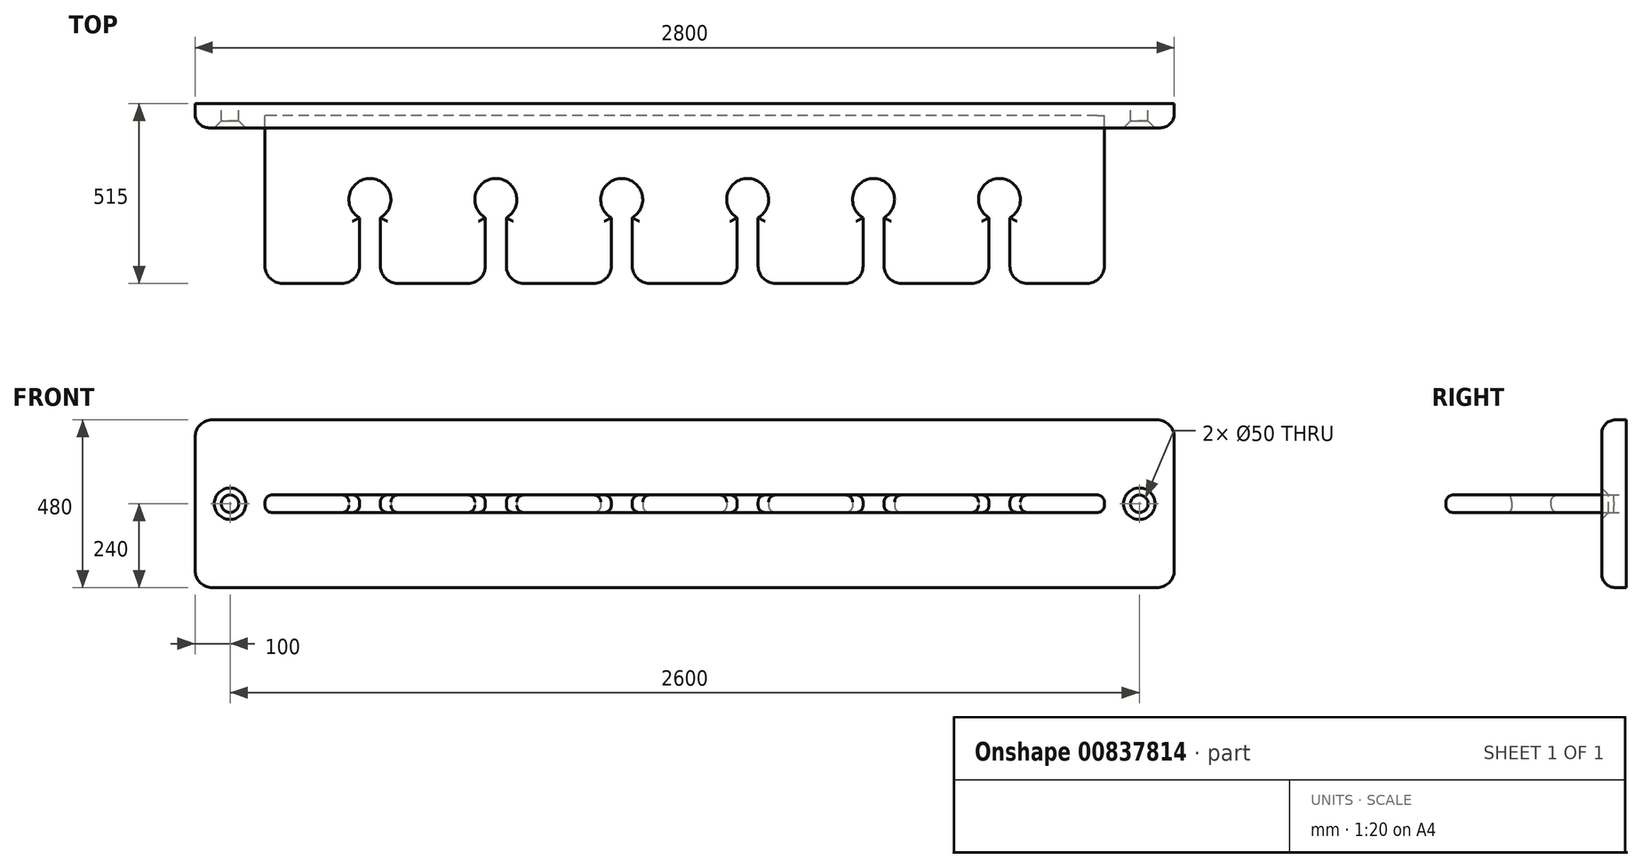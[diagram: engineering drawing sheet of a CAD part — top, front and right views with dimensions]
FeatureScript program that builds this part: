
annotation { "Feature Type Name" : "Feature", "Feature Type Description" : "" }
export const myFeature = defineFeature(function(context is Context, id is Id, definition is map)
    precondition{}
    {
        {
            assignVariable(context, id + "F0", {"name" : "size", "anyValue" : 2400 * mm});
        }
        {
            assignVariable(context, id + "F1", {"name" : "ratio", "anyValue" : 1 / 5});
        }
        {
            assignVariable(context, id + "F2", {"name" : "height", "anyValue" : getVariable(context, 'size') * getVariable(context, 'ratio')});
        }
        {
            assignVariable(context, id + "F3", {"name" : "thick", "anyValue" : 50 * mm});
        }
        {
            assignVariable(context, id + "F4", {"name" : "round", "anyValue" : 20 * mm});
        }
        {
            var Q0;
            Q0=qCreatedBy(makeId("Top.planeOp"),FACE);
            var sketch = newSketch(context, id + "F5", { "sketchPlane" : qUnion([Q0])});
            skLineSegment(sketch, "E0.top", {"start": v(1200, 240) * mm, "end": v(-1200, 240) * mm});
            skLineSegment(sketch, "E0.left", {"start": v(1200, -190) * mm, "end": v(1200, 240) * mm});
            skLineSegment(sketch, "E0.right", {"start": v(-1200, -190) * mm, "end": v(-1200, 240) * mm});
            skPoint(sketch, "E0.middle", {"position": v(0, 0) * mm});
            skArc(sketch, "E1", {"start": v(-870, -51.96) * mm, "mid": v(-900, 60) * mm, "end": v(-930, -51.96) * mm});
            skLineSegment(sketch, "E2", {"start": v(-930, -51.96) * mm, "end": v(-930, -190) * mm});
            skLineSegment(sketch, "E3", {"start": v(-870, -51.96) * mm, "end": v(-870, -190) * mm});
            skLineSegment(sketch, "E4.trimOffspring", {"start": v(-980, -240) * mm, "end": v(-1150, -240) * mm});
            skArc(sketch, "E5.1.0.0", {"start": v(-510, -51.96) * mm, "mid": v(-540, 60) * mm, "end": v(-570, -51.96) * mm});
            skLineSegment(sketch, "E5.1.0.1", {"start": v(-510, -51.96) * mm, "end": v(-510, -190) * mm});
            skLineSegment(sketch, "E5.1.0.2", {"start": v(-570, -51.96) * mm, "end": v(-570, -190) * mm});
            skArc(sketch, "E5.2.0.0", {"start": v(-150, -51.96) * mm, "mid": v(-180, 60) * mm, "end": v(-210, -51.96) * mm});
            skLineSegment(sketch, "E5.2.0.1", {"start": v(-150, -51.96) * mm, "end": v(-150, -190) * mm});
            skLineSegment(sketch, "E5.2.0.2", {"start": v(-210, -51.96) * mm, "end": v(-210, -190) * mm});
            skArc(sketch, "E5.3.0.0", {"start": v(210, -51.96) * mm, "mid": v(180, 60) * mm, "end": v(150, -51.96) * mm});
            skLineSegment(sketch, "E5.3.0.1", {"start": v(210, -51.96) * mm, "end": v(210, -190) * mm});
            skLineSegment(sketch, "E5.3.0.2", {"start": v(150, -51.96) * mm, "end": v(150, -190) * mm});
            skArc(sketch, "E5.4.0.0", {"start": v(570, -51.96) * mm, "mid": v(540, 60) * mm, "end": v(510, -51.96) * mm});
            skLineSegment(sketch, "E5.4.0.1", {"start": v(570, -51.96) * mm, "end": v(570, -190) * mm});
            skLineSegment(sketch, "E5.4.0.2", {"start": v(510, -51.96) * mm, "end": v(510, -190) * mm});
            skArc(sketch, "E5.5.0.0", {"start": v(930, -51.96) * mm, "mid": v(900, 60) * mm, "end": v(870, -51.96) * mm});
            skLineSegment(sketch, "E5.5.0.1", {"start": v(930, -51.96) * mm, "end": v(930, -190) * mm});
            skLineSegment(sketch, "E5.5.0.2", {"start": v(870, -51.96) * mm, "end": v(870, -190) * mm});
            skLineSegment(sketch, "E5.direction1", {"start": v(-900, 0) * mm, "end": v(-540, 0) * mm, "construction": true});
            skLineSegment(sketch, "E6.trimOffspring", {"start": v(-620, -240) * mm, "end": v(-820, -240) * mm});
            skLineSegment(sketch, "E7.trimOffspring", {"start": v(-260, -240) * mm, "end": v(-460, -240) * mm});
            skLineSegment(sketch, "E8.trimOffspring", {"start": v(100, -240) * mm, "end": v(-100, -240) * mm});
            skLineSegment(sketch, "E9.trimOffspring", {"start": v(460, -240) * mm, "end": v(260, -240) * mm});
            skLineSegment(sketch, "E10.trimOffspring", {"start": v(820, -240) * mm, "end": v(620, -240) * mm});
            skLineSegment(sketch, "E11", {"start": v(1150, -240) * mm, "end": v(980, -240) * mm});
            skPoint(sketch, "E12.visualSharp", {"position": v(-930, -240) * mm});
            skArc(sketch, "E12.filletArc", {"start": v(-980, -240) * mm, "mid": v(-944.64, -225.36) * mm, "end": v(-930, -190) * mm});
            skPoint(sketch, "E13.visualSharp", {"position": v(-870, -240) * mm});
            skArc(sketch, "E13.filletArc", {"start": v(-870, -190) * mm, "mid": v(-855.36, -225.36) * mm, "end": v(-820, -240) * mm});
            skPoint(sketch, "E14.visualSharp", {"position": v(-570, -240) * mm});
            skArc(sketch, "E14.filletArc", {"start": v(-620, -240) * mm, "mid": v(-584.64, -225.36) * mm, "end": v(-570, -190) * mm});
            skPoint(sketch, "E15.visualSharp", {"position": v(-510, -240) * mm});
            skArc(sketch, "E15.filletArc", {"start": v(-510, -190) * mm, "mid": v(-495.36, -225.36) * mm, "end": v(-460, -240) * mm});
            skPoint(sketch, "E16.visualSharp", {"position": v(-210, -240) * mm});
            skArc(sketch, "E16.filletArc", {"start": v(-260, -240) * mm, "mid": v(-224.64, -225.36) * mm, "end": v(-210, -190) * mm});
            skPoint(sketch, "E17.visualSharp", {"position": v(-150, -240) * mm});
            skArc(sketch, "E17.filletArc", {"start": v(-150, -190) * mm, "mid": v(-135.36, -225.36) * mm, "end": v(-100, -240) * mm});
            skPoint(sketch, "E18.visualSharp", {"position": v(150, -240) * mm});
            skArc(sketch, "E18.filletArc", {"start": v(100, -240) * mm, "mid": v(135.36, -225.36) * mm, "end": v(150, -190) * mm});
            skPoint(sketch, "E19.visualSharp", {"position": v(210, -240) * mm});
            skArc(sketch, "E19.filletArc", {"start": v(210, -190) * mm, "mid": v(224.64, -225.36) * mm, "end": v(260, -240) * mm});
            skPoint(sketch, "E20.visualSharp", {"position": v(510, -240) * mm});
            skArc(sketch, "E20.filletArc", {"start": v(460, -240) * mm, "mid": v(495.36, -225.36) * mm, "end": v(510, -190) * mm});
            skPoint(sketch, "E21.visualSharp", {"position": v(570, -240) * mm});
            skArc(sketch, "E21.filletArc", {"start": v(570, -190) * mm, "mid": v(584.64, -225.36) * mm, "end": v(620, -240) * mm});
            skPoint(sketch, "E22.visualSharp", {"position": v(870, -240) * mm});
            skArc(sketch, "E22.filletArc", {"start": v(820, -240) * mm, "mid": v(855.36, -225.36) * mm, "end": v(870, -190) * mm});
            skPoint(sketch, "E23.visualSharp", {"position": v(930, -240) * mm});
            skArc(sketch, "E23.filletArc", {"start": v(930, -190) * mm, "mid": v(944.64, -225.36) * mm, "end": v(980, -240) * mm});
            skPoint(sketch, "E24.visualSharp", {"position": v(-1200, -240) * mm});
            skArc(sketch, "E24.filletArc", {"start": v(-1200, -190) * mm, "mid": v(-1185.36, -225.36) * mm, "end": v(-1150, -240) * mm});
            skPoint(sketch, "E25.visualSharp", {"position": v(1200, -240) * mm});
            skArc(sketch, "E25.filletArc", {"start": v(1150, -240) * mm, "mid": v(1185.36, -225.36) * mm, "end": v(1200, -190) * mm});
            skSolve(sketch);
        }
        {
            var Q0;
            Q0=makeQuery(id+"F5.imprint","IMPRINT",FACE,{"disambiguationData":[TD([[makeQuery(id+"F5.imprint","IMPRINT",EDGE,{"derivedFrom":sQuery(id+"F5.wireOp",EDGE,"E0.top")}),1.0]])]});
            extrude(context, id + "F6", {"entities" : qUnion([Q0]), "endBound" : BoundingType.SYMMETRIC, "depth" : getVariable(context, 'thick'), "offsetDistance" : 25 * mm});
        }
        {
            var Q0;
            Q0=makeQuery(id+"F6.opExtrude","CAP_EDGE",EDGE,{"disambiguationData":[OSD([sQuery(id+"F5.wireOp",EDGE,"E6.trimOffspring")])],"isStart":false});
            var Q1;
            Q1=makeQuery(id+"F6.opExtrude","CAP_EDGE",EDGE,{"disambiguationData":[OSD([sQuery(id+"F5.wireOp",EDGE,"E2")])],"isStart":false});
            var Q2;
            Q2=makeQuery(id+"F6.opExtrude","CAP_EDGE",EDGE,{"disambiguationData":[OSD([sQuery(id+"F5.wireOp",EDGE,"E1")])],"isStart":false});
            var Q3;
            Q3=makeQuery(id+"F6.opExtrude","CAP_EDGE",EDGE,{"disambiguationData":[OSD([sQuery(id+"F5.wireOp",EDGE,"E12.filletArc")])],"isStart":false});
            var Q4;
            Q4=makeQuery(id+"F6.opExtrude","CAP_EDGE",EDGE,{"disambiguationData":[OSD([sQuery(id+"F5.wireOp",EDGE,"E4.trimOffspring")])],"isStart":false});
            var Q5;
            Q5=makeQuery(id+"F6.opExtrude","CAP_EDGE",EDGE,{"disambiguationData":[OSD([sQuery(id+"F5.wireOp",EDGE,"E24.filletArc")])],"isStart":false});
            var Q6;
            Q6=makeQuery(id+"F6.opExtrude","CAP_EDGE",EDGE,{"disambiguationData":[OSD([sQuery(id+"F5.wireOp",EDGE,"E0.right")])],"isStart":false});
            var Q7;
            Q7=makeQuery(id+"F6.opExtrude","CAP_EDGE",EDGE,{"disambiguationData":[OSD([sQuery(id+"F5.wireOp",EDGE,"E14.filletArc")])],"isStart":false});
            var Q8;
            Q8=makeQuery(id+"F6.opExtrude","CAP_EDGE",EDGE,{"disambiguationData":[OSD([sQuery(id+"F5.wireOp",EDGE,"E5.1.0.2")])],"isStart":false});
            var Q9;
            Q9=makeQuery(id+"F6.opExtrude","CAP_EDGE",EDGE,{"disambiguationData":[OSD([sQuery(id+"F5.wireOp",EDGE,"E5.1.0.0")])],"isStart":false});
            var Q10;
            Q10=makeQuery(id+"F6.opExtrude","CAP_EDGE",EDGE,{"disambiguationData":[OSD([sQuery(id+"F5.wireOp",EDGE,"E5.1.0.1")])],"isStart":false});
            var Q11;
            Q11=makeQuery(id+"F6.opExtrude","CAP_EDGE",EDGE,{"disambiguationData":[OSD([sQuery(id+"F5.wireOp",EDGE,"E15.filletArc")])],"isStart":false});
            var Q12;
            Q12=makeQuery(id+"F6.opExtrude","CAP_EDGE",EDGE,{"disambiguationData":[OSD([sQuery(id+"F5.wireOp",EDGE,"E7.trimOffspring")])],"isStart":false});
            var Q13;
            Q13=makeQuery(id+"F6.opExtrude","CAP_EDGE",EDGE,{"disambiguationData":[OSD([sQuery(id+"F5.wireOp",EDGE,"E16.filletArc")])],"isStart":false});
            var Q14;
            Q14=makeQuery(id+"F6.opExtrude","CAP_EDGE",EDGE,{"disambiguationData":[OSD([sQuery(id+"F5.wireOp",EDGE,"E5.2.0.2")])],"isStart":false});
            var Q15;
            Q15=makeQuery(id+"F6.opExtrude","CAP_EDGE",EDGE,{"disambiguationData":[OSD([sQuery(id+"F5.wireOp",EDGE,"E5.2.0.0")])],"isStart":false});
            var Q16;
            Q16=makeQuery(id+"F6.opExtrude","CAP_EDGE",EDGE,{"disambiguationData":[OSD([sQuery(id+"F5.wireOp",EDGE,"E5.2.0.1")])],"isStart":false});
            var Q17;
            Q17=makeQuery(id+"F6.opExtrude","CAP_EDGE",EDGE,{"disambiguationData":[OSD([sQuery(id+"F5.wireOp",EDGE,"E17.filletArc")])],"isStart":false});
            var Q18;
            Q18=makeQuery(id+"F6.opExtrude","CAP_EDGE",EDGE,{"disambiguationData":[OSD([sQuery(id+"F5.wireOp",EDGE,"E8.trimOffspring")])],"isStart":false});
            var Q19;
            Q19=makeQuery(id+"F6.opExtrude","CAP_EDGE",EDGE,{"disambiguationData":[OSD([sQuery(id+"F5.wireOp",EDGE,"E18.filletArc")])],"isStart":false});
            var Q20;
            Q20=makeQuery(id+"F6.opExtrude","CAP_EDGE",EDGE,{"disambiguationData":[OSD([sQuery(id+"F5.wireOp",EDGE,"E5.3.0.2")])],"isStart":false});
            var Q21;
            Q21=makeQuery(id+"F6.opExtrude","CAP_EDGE",EDGE,{"disambiguationData":[OSD([sQuery(id+"F5.wireOp",EDGE,"E5.3.0.0")])],"isStart":false});
            var Q22;
            Q22=makeQuery(id+"F6.opExtrude","CAP_EDGE",EDGE,{"disambiguationData":[OSD([sQuery(id+"F5.wireOp",EDGE,"E5.3.0.1")])],"isStart":false});
            var Q23;
            Q23=makeQuery(id+"F6.opExtrude","CAP_EDGE",EDGE,{"disambiguationData":[OSD([sQuery(id+"F5.wireOp",EDGE,"E19.filletArc")])],"isStart":false});
            var Q24;
            Q24=makeQuery(id+"F6.opExtrude","CAP_EDGE",EDGE,{"disambiguationData":[OSD([sQuery(id+"F5.wireOp",EDGE,"E9.trimOffspring")])],"isStart":false});
            var Q25;
            Q25=makeQuery(id+"F6.opExtrude","CAP_EDGE",EDGE,{"disambiguationData":[OSD([sQuery(id+"F5.wireOp",EDGE,"E20.filletArc")])],"isStart":false});
            var Q26;
            Q26=makeQuery(id+"F6.opExtrude","CAP_EDGE",EDGE,{"disambiguationData":[OSD([sQuery(id+"F5.wireOp",EDGE,"E5.4.0.2")])],"isStart":false});
            var Q27;
            Q27=makeQuery(id+"F6.opExtrude","CAP_EDGE",EDGE,{"disambiguationData":[OSD([sQuery(id+"F5.wireOp",EDGE,"E5.4.0.0")])],"isStart":false});
            var Q28;
            Q28=makeQuery(id+"F6.opExtrude","CAP_EDGE",EDGE,{"disambiguationData":[OSD([sQuery(id+"F5.wireOp",EDGE,"E5.4.0.1")])],"isStart":false});
            var Q29;
            Q29=makeQuery(id+"F6.opExtrude","CAP_EDGE",EDGE,{"disambiguationData":[OSD([sQuery(id+"F5.wireOp",EDGE,"E21.filletArc")])],"isStart":false});
            var Q30;
            Q30=makeQuery(id+"F6.opExtrude","CAP_EDGE",EDGE,{"disambiguationData":[OSD([sQuery(id+"F5.wireOp",EDGE,"E10.trimOffspring")])],"isStart":false});
            var Q31;
            Q31=makeQuery(id+"F6.opExtrude","CAP_EDGE",EDGE,{"disambiguationData":[OSD([sQuery(id+"F5.wireOp",EDGE,"E22.filletArc")])],"isStart":false});
            var Q32;
            Q32=makeQuery(id+"F6.opExtrude","CAP_EDGE",EDGE,{"disambiguationData":[OSD([sQuery(id+"F5.wireOp",EDGE,"E5.5.0.2")])],"isStart":false});
            var Q33;
            Q33=makeQuery(id+"F6.opExtrude","CAP_EDGE",EDGE,{"disambiguationData":[OSD([sQuery(id+"F5.wireOp",EDGE,"E5.5.0.0")])],"isStart":false});
            var Q34;
            Q34=makeQuery(id+"F6.opExtrude","CAP_EDGE",EDGE,{"disambiguationData":[OSD([sQuery(id+"F5.wireOp",EDGE,"E5.5.0.1")])],"isStart":false});
            var Q35;
            Q35=makeQuery(id+"F6.opExtrude","CAP_EDGE",EDGE,{"disambiguationData":[OSD([sQuery(id+"F5.wireOp",EDGE,"E23.filletArc")])],"isStart":false});
            var Q36;
            Q36=makeQuery(id+"F6.opExtrude","CAP_EDGE",EDGE,{"disambiguationData":[OSD([sQuery(id+"F5.wireOp",EDGE,"E11")])],"isStart":false});
            var Q37;
            Q37=makeQuery(id+"F6.opExtrude","CAP_EDGE",EDGE,{"disambiguationData":[OSD([sQuery(id+"F5.wireOp",EDGE,"E25.filletArc")])],"isStart":false});
            var Q38;
            Q38=makeQuery(id+"F6.opExtrude","CAP_EDGE",EDGE,{"disambiguationData":[OSD([sQuery(id+"F5.wireOp",EDGE,"E0.left")])],"isStart":false});
            var Q39;
            Q39=makeQuery(id+"F6.opExtrude","CAP_EDGE",EDGE,{"disambiguationData":[OSD([sQuery(id+"F5.wireOp",EDGE,"E11")])],"isStart":true});
            var Q40;
            Q40=makeQuery(id+"F6.opExtrude","CAP_EDGE",EDGE,{"disambiguationData":[OSD([sQuery(id+"F5.wireOp",EDGE,"E25.filletArc")])],"isStart":true});
            var Q41;
            Q41=makeQuery(id+"F6.opExtrude","CAP_EDGE",EDGE,{"disambiguationData":[OSD([sQuery(id+"F5.wireOp",EDGE,"E0.left")])],"isStart":true});
            var Q42;
            Q42=makeQuery(id+"F6.opExtrude","CAP_EDGE",EDGE,{"disambiguationData":[OSD([sQuery(id+"F5.wireOp",EDGE,"E23.filletArc")])],"isStart":true});
            var Q43;
            Q43=makeQuery(id+"F6.opExtrude","CAP_EDGE",EDGE,{"disambiguationData":[OSD([sQuery(id+"F5.wireOp",EDGE,"E5.5.0.1")])],"isStart":true});
            var Q44;
            Q44=makeQuery(id+"F6.opExtrude","CAP_EDGE",EDGE,{"disambiguationData":[OSD([sQuery(id+"F5.wireOp",EDGE,"E5.5.0.0")])],"isStart":true});
            var Q45;
            Q45=makeQuery(id+"F6.opExtrude","CAP_EDGE",EDGE,{"disambiguationData":[OSD([sQuery(id+"F5.wireOp",EDGE,"E5.5.0.2")])],"isStart":true});
            var Q46;
            Q46=makeQuery(id+"F6.opExtrude","CAP_EDGE",EDGE,{"disambiguationData":[OSD([sQuery(id+"F5.wireOp",EDGE,"E22.filletArc")])],"isStart":true});
            var Q47;
            Q47=makeQuery(id+"F6.opExtrude","CAP_EDGE",EDGE,{"disambiguationData":[OSD([sQuery(id+"F5.wireOp",EDGE,"E10.trimOffspring")])],"isStart":true});
            var Q48;
            Q48=makeQuery(id+"F6.opExtrude","CAP_EDGE",EDGE,{"disambiguationData":[OSD([sQuery(id+"F5.wireOp",EDGE,"E21.filletArc")])],"isStart":true});
            var Q49;
            Q49=makeQuery(id+"F6.opExtrude","CAP_EDGE",EDGE,{"disambiguationData":[OSD([sQuery(id+"F5.wireOp",EDGE,"E5.4.0.1")])],"isStart":true});
            var Q50;
            Q50=makeQuery(id+"F6.opExtrude","CAP_EDGE",EDGE,{"disambiguationData":[OSD([sQuery(id+"F5.wireOp",EDGE,"E5.4.0.0")])],"isStart":true});
            var Q51;
            Q51=makeQuery(id+"F6.opExtrude","CAP_EDGE",EDGE,{"disambiguationData":[OSD([sQuery(id+"F5.wireOp",EDGE,"E5.4.0.2")])],"isStart":true});
            var Q52;
            Q52=makeQuery(id+"F6.opExtrude","CAP_EDGE",EDGE,{"disambiguationData":[OSD([sQuery(id+"F5.wireOp",EDGE,"E20.filletArc")])],"isStart":true});
            var Q53;
            Q53=makeQuery(id+"F6.opExtrude","CAP_EDGE",EDGE,{"disambiguationData":[OSD([sQuery(id+"F5.wireOp",EDGE,"E9.trimOffspring")])],"isStart":true});
            var Q54;
            Q54=makeQuery(id+"F6.opExtrude","CAP_EDGE",EDGE,{"disambiguationData":[OSD([sQuery(id+"F5.wireOp",EDGE,"E19.filletArc")])],"isStart":true});
            var Q55;
            Q55=makeQuery(id+"F6.opExtrude","CAP_EDGE",EDGE,{"disambiguationData":[OSD([sQuery(id+"F5.wireOp",EDGE,"E5.3.0.1")])],"isStart":true});
            var Q56;
            Q56=makeQuery(id+"F6.opExtrude","CAP_EDGE",EDGE,{"disambiguationData":[OSD([sQuery(id+"F5.wireOp",EDGE,"E5.3.0.0")])],"isStart":true});
            var Q57;
            Q57=makeQuery(id+"F6.opExtrude","CAP_EDGE",EDGE,{"disambiguationData":[OSD([sQuery(id+"F5.wireOp",EDGE,"E5.3.0.2")])],"isStart":true});
            var Q58;
            Q58=makeQuery(id+"F6.opExtrude","CAP_EDGE",EDGE,{"disambiguationData":[OSD([sQuery(id+"F5.wireOp",EDGE,"E18.filletArc")])],"isStart":true});
            var Q59;
            Q59=makeQuery(id+"F6.opExtrude","CAP_EDGE",EDGE,{"disambiguationData":[OSD([sQuery(id+"F5.wireOp",EDGE,"E8.trimOffspring")])],"isStart":true});
            var Q60;
            Q60=makeQuery(id+"F6.opExtrude","CAP_EDGE",EDGE,{"disambiguationData":[OSD([sQuery(id+"F5.wireOp",EDGE,"E17.filletArc")])],"isStart":true});
            var Q61;
            Q61=makeQuery(id+"F6.opExtrude","CAP_EDGE",EDGE,{"disambiguationData":[OSD([sQuery(id+"F5.wireOp",EDGE,"E5.2.0.1")])],"isStart":true});
            var Q62;
            Q62=makeQuery(id+"F6.opExtrude","CAP_EDGE",EDGE,{"disambiguationData":[OSD([sQuery(id+"F5.wireOp",EDGE,"E5.2.0.0")])],"isStart":true});
            var Q63;
            Q63=makeQuery(id+"F6.opExtrude","CAP_EDGE",EDGE,{"disambiguationData":[OSD([sQuery(id+"F5.wireOp",EDGE,"E5.2.0.2")])],"isStart":true});
            var Q64;
            Q64=makeQuery(id+"F6.opExtrude","CAP_EDGE",EDGE,{"disambiguationData":[OSD([sQuery(id+"F5.wireOp",EDGE,"E16.filletArc")])],"isStart":true});
            var Q65;
            Q65=makeQuery(id+"F6.opExtrude","CAP_EDGE",EDGE,{"disambiguationData":[OSD([sQuery(id+"F5.wireOp",EDGE,"E7.trimOffspring")])],"isStart":true});
            var Q66;
            Q66=makeQuery(id+"F6.opExtrude","CAP_EDGE",EDGE,{"disambiguationData":[OSD([sQuery(id+"F5.wireOp",EDGE,"E15.filletArc")])],"isStart":true});
            var Q67;
            Q67=makeQuery(id+"F6.opExtrude","CAP_EDGE",EDGE,{"disambiguationData":[OSD([sQuery(id+"F5.wireOp",EDGE,"E5.1.0.1")])],"isStart":true});
            var Q68;
            Q68=makeQuery(id+"F6.opExtrude","CAP_EDGE",EDGE,{"disambiguationData":[OSD([sQuery(id+"F5.wireOp",EDGE,"E5.1.0.0")])],"isStart":true});
            var Q69;
            Q69=makeQuery(id+"F6.opExtrude","CAP_EDGE",EDGE,{"disambiguationData":[OSD([sQuery(id+"F5.wireOp",EDGE,"E5.1.0.2")])],"isStart":true});
            var Q70;
            Q70=makeQuery(id+"F6.opExtrude","CAP_EDGE",EDGE,{"disambiguationData":[OSD([sQuery(id+"F5.wireOp",EDGE,"E14.filletArc")])],"isStart":true});
            var Q71;
            Q71=makeQuery(id+"F6.opExtrude","CAP_EDGE",EDGE,{"disambiguationData":[OSD([sQuery(id+"F5.wireOp",EDGE,"E6.trimOffspring")])],"isStart":true});
            var Q72;
            Q72=makeQuery(id+"F6.opExtrude","CAP_EDGE",EDGE,{"disambiguationData":[OSD([sQuery(id+"F5.wireOp",EDGE,"E13.filletArc")])],"isStart":true});
            var Q73;
            Q73=makeQuery(id+"F6.opExtrude","CAP_EDGE",EDGE,{"disambiguationData":[OSD([sQuery(id+"F5.wireOp",EDGE,"E3")])],"isStart":true});
            var Q74;
            Q74=makeQuery(id+"F6.opExtrude","CAP_EDGE",EDGE,{"disambiguationData":[OSD([sQuery(id+"F5.wireOp",EDGE,"E1")])],"isStart":true});
            var Q75;
            Q75=makeQuery(id+"F6.opExtrude","CAP_EDGE",EDGE,{"disambiguationData":[OSD([sQuery(id+"F5.wireOp",EDGE,"E2")])],"isStart":true});
            var Q76;
            Q76=makeQuery(id+"F6.opExtrude","CAP_EDGE",EDGE,{"disambiguationData":[OSD([sQuery(id+"F5.wireOp",EDGE,"E12.filletArc")])],"isStart":true});
            var Q77;
            Q77=makeQuery(id+"F6.opExtrude","CAP_EDGE",EDGE,{"disambiguationData":[OSD([sQuery(id+"F5.wireOp",EDGE,"E4.trimOffspring")])],"isStart":true});
            var Q78;
            Q78=makeQuery(id+"F6.opExtrude","CAP_EDGE",EDGE,{"disambiguationData":[OSD([sQuery(id+"F5.wireOp",EDGE,"E24.filletArc")])],"isStart":true});
            var Q79;
            Q79=makeQuery(id+"F6.opExtrude","CAP_EDGE",EDGE,{"disambiguationData":[OSD([sQuery(id+"F5.wireOp",EDGE,"E0.right")])],"isStart":true});
            fillet(context, id + "F7", {"entities" : qUnion([Q0, Q1, Q2, Q3, Q4, Q5, Q6, Q7, Q8, Q9, Q10, Q11, Q12, Q13, Q14, Q15, Q16, Q17, Q18, Q19, Q20, Q21, Q22, Q23, Q24, Q25, Q26, Q27, Q28, Q29, Q30, Q31, Q32, Q33, Q34, Q35, Q36, Q37, Q38, Q39, Q40, Q41, Q42, Q43, Q44, Q45, Q46, Q47, Q48, Q49, Q50, Q51, Q52, Q53, Q54, Q55, Q56, Q57, Q58, Q59, Q60, Q61, Q62, Q63, Q64, Q65, Q66, Q67, Q68, Q69, Q70, Q71, Q72, Q73, Q74, Q75, Q76, Q77, Q78, Q79]), "radius" : getVariable(context, 'round'), "tangentPropagation" : true, "allowEdgeOverflow" : false});
        }
        {
            var Q0;
            Q0=qCreatedBy(makeId("Front.planeOp"),FACE);
            cPlane(context, id + "F8", {"entities" : qUnion([Q0]), "cplaneType" : CPlaneType.OFFSET, "offset" : getVariable(context, 'height') / 2, "oppositeDirection" : true, "width" : 150 * mm, "height" : 150 * mm});
        }
        {
            var Q0;
            Q0=qCreatedBy(id+"F8.planeOp",FACE);
            var sketch = newSketch(context, id + "F9", { "sketchPlane" : qUnion([Q0])});
            skLineSegment(sketch, "E26.bottom", {"start": v(1350, -240) * mm, "end": v(-1350, -240) * mm});
            skLineSegment(sketch, "E26.top", {"start": v(1350, 240) * mm, "end": v(-1350, 240) * mm});
            skLineSegment(sketch, "E26.left", {"start": v(1400, -190) * mm, "end": v(1400, 190) * mm});
            skLineSegment(sketch, "E26.right", {"start": v(-1400, -190) * mm, "end": v(-1400, 190) * mm});
            skPoint(sketch, "E26.middle", {"position": v(0, 0) * mm});
            skPoint(sketch, "E27.visualSharp", {"position": v(-1400, 240) * mm});
            skArc(sketch, "E27.filletArc", {"start": v(-1350, 240) * mm, "mid": v(-1385.36, 225.36) * mm, "end": v(-1400, 190) * mm});
            skPoint(sketch, "E28.visualSharp", {"position": v(1400, 240) * mm});
            skArc(sketch, "E28.filletArc", {"start": v(1400, 190) * mm, "mid": v(1385.36, 225.36) * mm, "end": v(1350, 240) * mm});
            skPoint(sketch, "E29.visualSharp", {"position": v(1400, -240) * mm});
            skArc(sketch, "E29.filletArc", {"start": v(1350, -240) * mm, "mid": v(1385.36, -225.36) * mm, "end": v(1400, -190) * mm});
            skPoint(sketch, "E30.visualSharp", {"position": v(-1400, -240) * mm});
            skArc(sketch, "E30.filletArc", {"start": v(-1400, -190) * mm, "mid": v(-1385.36, -225.36) * mm, "end": v(-1350, -240) * mm});
            skCircle(sketch, "E31", {"center": v(-1300, 0) * mm, "radius": 25 * mm});
            skCircle(sketch, "E32", {"center": v(1300, 0) * mm, "radius": 25 * mm});
            skSolve(sketch);
        }
        {
            var Q0;
            Q0 = qSketchRegion(id + "F9", true);
            extrude(context, id + "F10", {"entities" : qUnion([Q0]), "endBound" : BoundingType.SYMMETRIC, "depth" : 70 * mm, "offsetDistance" : 25 * mm});
        }
        {
            var Q0;
            Q0=makeQuery(id+"F6.opExtrude","SWEPT_BODY",BODY,{"disambiguationData":[OSD([sQuery(id+"F5.wireOp",EDGE,"E0.top"),sQuery(id+"F5.wireOp",EDGE,"E0.left"),sQuery(id+"F5.wireOp",EDGE,"E0.right"),sQuery(id+"F5.wireOp",EDGE,"E1"),sQuery(id+"F5.wireOp",EDGE,"E2"),sQuery(id+"F5.wireOp",EDGE,"E3"),sQuery(id+"F5.wireOp",EDGE,"E4.trimOffspring"),sQuery(id+"F5.wireOp",EDGE,"E5.1.0.0"),sQuery(id+"F5.wireOp",EDGE,"E5.1.0.1"),sQuery(id+"F5.wireOp",EDGE,"E5.1.0.2"),sQuery(id+"F5.wireOp",EDGE,"E5.2.0.0"),sQuery(id+"F5.wireOp",EDGE,"E5.2.0.1"),sQuery(id+"F5.wireOp",EDGE,"E5.2.0.2"),sQuery(id+"F5.wireOp",EDGE,"E5.3.0.0"),sQuery(id+"F5.wireOp",EDGE,"E5.3.0.1"),sQuery(id+"F5.wireOp",EDGE,"E5.3.0.2"),sQuery(id+"F5.wireOp",EDGE,"E5.4.0.0"),sQuery(id+"F5.wireOp",EDGE,"E5.4.0.1"),sQuery(id+"F5.wireOp",EDGE,"E5.4.0.2"),sQuery(id+"F5.wireOp",EDGE,"E5.5.0.0"),sQuery(id+"F5.wireOp",EDGE,"E5.5.0.1"),sQuery(id+"F5.wireOp",EDGE,"E5.5.0.2"),sQuery(id+"F5.wireOp",EDGE,"E6.trimOffspring"),sQuery(id+"F5.wireOp",EDGE,"E7.trimOffspring"),sQuery(id+"F5.wireOp",EDGE,"E8.trimOffspring"),sQuery(id+"F5.wireOp",EDGE,"E9.trimOffspring"),sQuery(id+"F5.wireOp",EDGE,"E10.trimOffspring"),sQuery(id+"F5.wireOp",EDGE,"E11"),sQuery(id+"F5.wireOp",EDGE,"E12.filletArc"),sQuery(id+"F5.wireOp",EDGE,"E13.filletArc"),sQuery(id+"F5.wireOp",EDGE,"E14.filletArc"),sQuery(id+"F5.wireOp",EDGE,"E15.filletArc"),sQuery(id+"F5.wireOp",EDGE,"E16.filletArc"),sQuery(id+"F5.wireOp",EDGE,"E17.filletArc"),sQuery(id+"F5.wireOp",EDGE,"E18.filletArc"),sQuery(id+"F5.wireOp",EDGE,"E19.filletArc"),sQuery(id+"F5.wireOp",EDGE,"E20.filletArc"),sQuery(id+"F5.wireOp",EDGE,"E21.filletArc"),sQuery(id+"F5.wireOp",EDGE,"E22.filletArc"),sQuery(id+"F5.wireOp",EDGE,"E23.filletArc"),sQuery(id+"F5.wireOp",EDGE,"E24.filletArc"),sQuery(id+"F5.wireOp",EDGE,"E25.filletArc")])]});
            var Q1;
            Q1=makeQuery(id+"F10.opExtrude","SWEPT_BODY",BODY,{"disambiguationData":[OSD([sQuery(id+"F9.wireOp",EDGE,"E26.bottom"),sQuery(id+"F9.wireOp",EDGE,"E26.top"),sQuery(id+"F9.wireOp",EDGE,"E26.left"),sQuery(id+"F9.wireOp",EDGE,"E26.right"),sQuery(id+"F9.wireOp",EDGE,"E27.filletArc"),sQuery(id+"F9.wireOp",EDGE,"E28.filletArc"),sQuery(id+"F9.wireOp",EDGE,"E29.filletArc"),sQuery(id+"F9.wireOp",EDGE,"E30.filletArc")])]});
            booleanBodies(context, id + "F11", {"operationType" : BooleanOperationType.SUBTRACTION, "tools" : qUnion([Q0]), "targets" : qUnion([Q1]), "keepTools" : true});
        }
        {
            var Q0;
            Q0=makeQuery(id+"F10.opExtrude","CAP_EDGE",EDGE,{"disambiguationData":[OSD([sQuery(id+"F9.wireOp",EDGE,"E26.bottom")])],"isStart":false});
            var Q1;
            Q1=makeQuery(id+"F10.opExtrude","CAP_EDGE",EDGE,{"disambiguationData":[OSD([sQuery(id+"F9.wireOp",EDGE,"E26.right")])],"isStart":false});
            var Q2;
            Q2=makeQuery(id+"F10.opExtrude","CAP_EDGE",EDGE,{"disambiguationData":[OSD([sQuery(id+"F9.wireOp",EDGE,"E30.filletArc")])],"isStart":false});
            var Q3;
            Q3=makeQuery(id+"F10.opExtrude","CAP_EDGE",EDGE,{"disambiguationData":[OSD([sQuery(id+"F9.wireOp",EDGE,"E27.filletArc")])],"isStart":false});
            var Q4;
            Q4=makeQuery(id+"F10.opExtrude","CAP_EDGE",EDGE,{"disambiguationData":[OSD([sQuery(id+"F9.wireOp",EDGE,"E26.top")])],"isStart":false});
            var Q5;
            Q5=makeQuery(id+"F10.opExtrude","CAP_EDGE",EDGE,{"disambiguationData":[OSD([sQuery(id+"F9.wireOp",EDGE,"E28.filletArc")])],"isStart":false});
            var Q6;
            Q6=makeQuery(id+"F10.opExtrude","CAP_EDGE",EDGE,{"disambiguationData":[OSD([sQuery(id+"F9.wireOp",EDGE,"E26.left")])],"isStart":false});
            var Q7;
            Q7=makeQuery(id+"F10.opExtrude","CAP_EDGE",EDGE,{"disambiguationData":[OSD([sQuery(id+"F9.wireOp",EDGE,"E29.filletArc")])],"isStart":false});
            fillet(context, id + "F12", {"entities" : qUnion([Q0, Q1, Q2, Q3, Q4, Q5, Q6, Q7]), "radius" : 40 * mm, "tangentPropagation" : true, "allowEdgeOverflow" : false});
        }
        {
            var Q0;
            Q0=makeQuery(id+"F10.opExtrude","CAP_EDGE",EDGE,{"disambiguationData":[OSD([sQuery(id+"F9.wireOp",EDGE,"E31")])],"isStart":false});
            var Q1;
            Q1=makeQuery(id+"F10.opExtrude","CAP_EDGE",EDGE,{"disambiguationData":[OSD([sQuery(id+"F9.wireOp",EDGE,"E32")])],"isStart":false});
            chamfer(context, id + "F13", {"entities" : qUnion([Q0, Q1]), "width" : 20 * mm, "tangentPropagation" : true});
        }
    });
